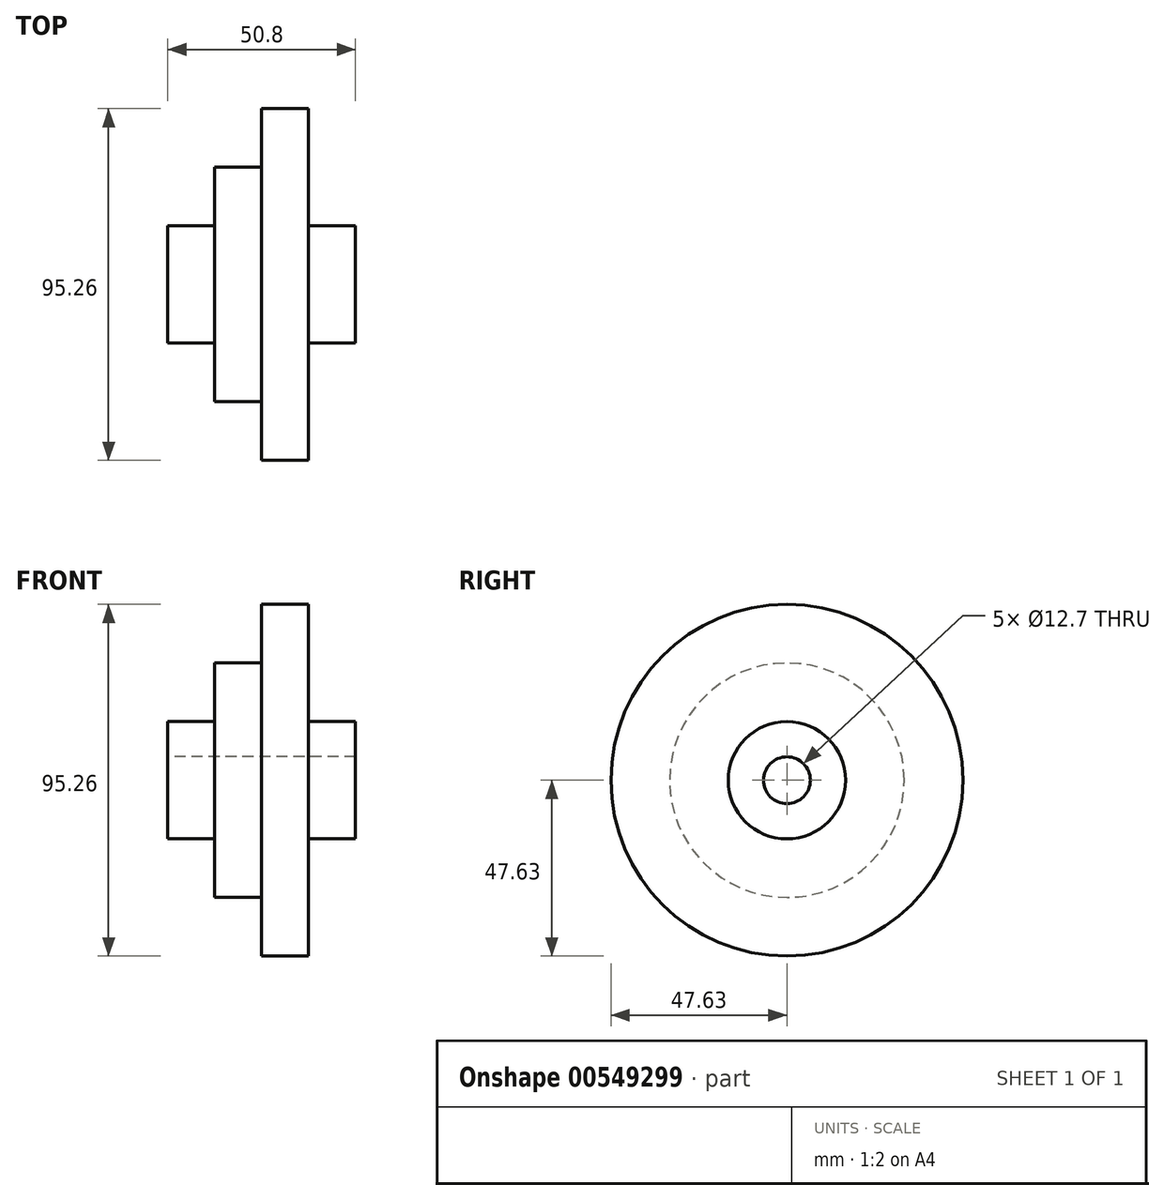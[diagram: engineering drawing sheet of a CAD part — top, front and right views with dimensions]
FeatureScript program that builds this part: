
annotation { "Feature Type Name" : "Feature", "Feature Type Description" : "" }
export const myFeature = defineFeature(function(context is Context, id is Id, definition is map)
    precondition{}
    {
        {
            var Q0;
            Q0=qCreatedBy(makeId("Front.planeOp"),FACE);
            var sketch = newSketch(context, id + "F0", { "sketchPlane" : qUnion([Q0])});
            skLineSegment(sketch, "E0", {"start": v(0, 0) * mm, "end": v(-59.94, 0) * mm, "construction": true});
            skLineSegment(sketch, "E1", {"start": v(-50.8, 0) * mm, "end": v(-50.8, 15.88) * mm});
            skLineSegment(sketch, "E2", {"start": v(-50.8, 15.88) * mm, "end": v(-38.1, 15.88) * mm});
            skLineSegment(sketch, "E3", {"start": v(-38.1, 15.88) * mm, "end": v(-38.1, 31.75) * mm});
            skLineSegment(sketch, "E4", {"start": v(-38.1, 31.75) * mm, "end": v(-25.4, 31.75) * mm});
            skLineSegment(sketch, "E5", {"start": v(-25.4, 31.75) * mm, "end": v(-25.4, 47.63) * mm});
            skLineSegment(sketch, "E6", {"start": v(-25.4, 47.63) * mm, "end": v(-12.7, 47.63) * mm});
            skLineSegment(sketch, "E7", {"start": v(-12.7, 47.63) * mm, "end": v(-12.7, 15.88) * mm});
            skLineSegment(sketch, "E8", {"start": v(-12.7, 15.88) * mm, "end": v(0, 15.88) * mm});
            skLineSegment(sketch, "E9", {"start": v(0, 15.88) * mm, "end": v(0, 0) * mm});
            skLineSegment(sketch, "E10", {"start": v(0, 0) * mm, "end": v(-50.8, 0) * mm});
            skSolve(sketch);
        }
        {
            var Q0;
            Q0=makeQuery(id+"F0.imprint","IMPRINT",FACE,{"disambiguationData":[TD([[makeQuery(id+"F0.imprint","IMPRINT",EDGE,{"derivedFrom":sQuery(id+"F0.wireOp",EDGE,"E1")}),-1.0]])]});
            var Q1;
            Q1=sQuery(id+"F0.wireOp",EDGE,"E0");
            revolve(context, id + "F1", {"entities" : qUnion([Q0]), "axis" : qUnion([Q1]), "revolveType" : RevolveType.FULL});
        }
        {
            var Q0;
            Q0=makeQuery(id+"F1.opRevolve","SWEPT_FACE",FACE,{"disambiguationData":[OSD([sQuery(id+"F0.wireOp",EDGE,"E1")])]});
            var sketch = newSketch(context, id + "F2", { "sketchPlane" : qUnion([Q0])});
            skCircle(sketch, "E11", {"center": v(0, 0) * mm, "radius": 6.35 * mm});
            skSolve(sketch);
        }
        {
            var Q0;
            Q0=makeQuery(id+"F2.imprint","IMPRINT",FACE,{"disambiguationData":[TD([[makeQuery(id+"F2.imprint","IMPRINT",EDGE,{"derivedFrom":sQuery(id+"F2.wireOp",EDGE,"E11")}),1.0]])]});
            extrude(context, id + "F3", {"entities" : qUnion([Q0]), "operationType" : NewBodyOperationType.REMOVE, "oppositeDirection" : true, "depth" : 50.8 * mm, "offsetDistance" : 25.4 * mm});
        }
    });
